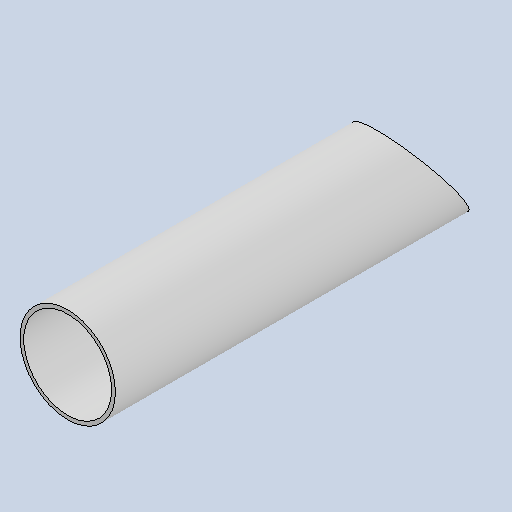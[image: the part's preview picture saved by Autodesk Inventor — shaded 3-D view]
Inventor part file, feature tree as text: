
AUTODESK INVENTOR PART (.ipt)
format: ipt  version: 2025 (Build 290162010, 162A)  size: 109,056 bytes
history: native  units: mm
features: extrude x2, sketch x2, projected_geometry x1
ambient origin geometry x8: Origin, YZ Plane, XZ Plane, XY Plane, X Axis, Y Axis, Z Axis, Center Point
bodies: Solid1 (feature_tree)
feature tree (5):
  extrude  "Extrusion1"  Depth=3.0mm
  extrude  "Extrusion2"  Depth=300.0mm
  sketch  "Sketch1"  dims[d0=76.0mm d1=3.0mm]
  sketch  "Sketch2"  dims[d2=300.0mm d3=0.0mm d4=6.108652mm d5=300.0mm d6=0.0mm d7=246.784227mm d8=300.0mm d9=300.0mm d10=546.784227mm]
  projected_geometry  "Projected Loop1"
